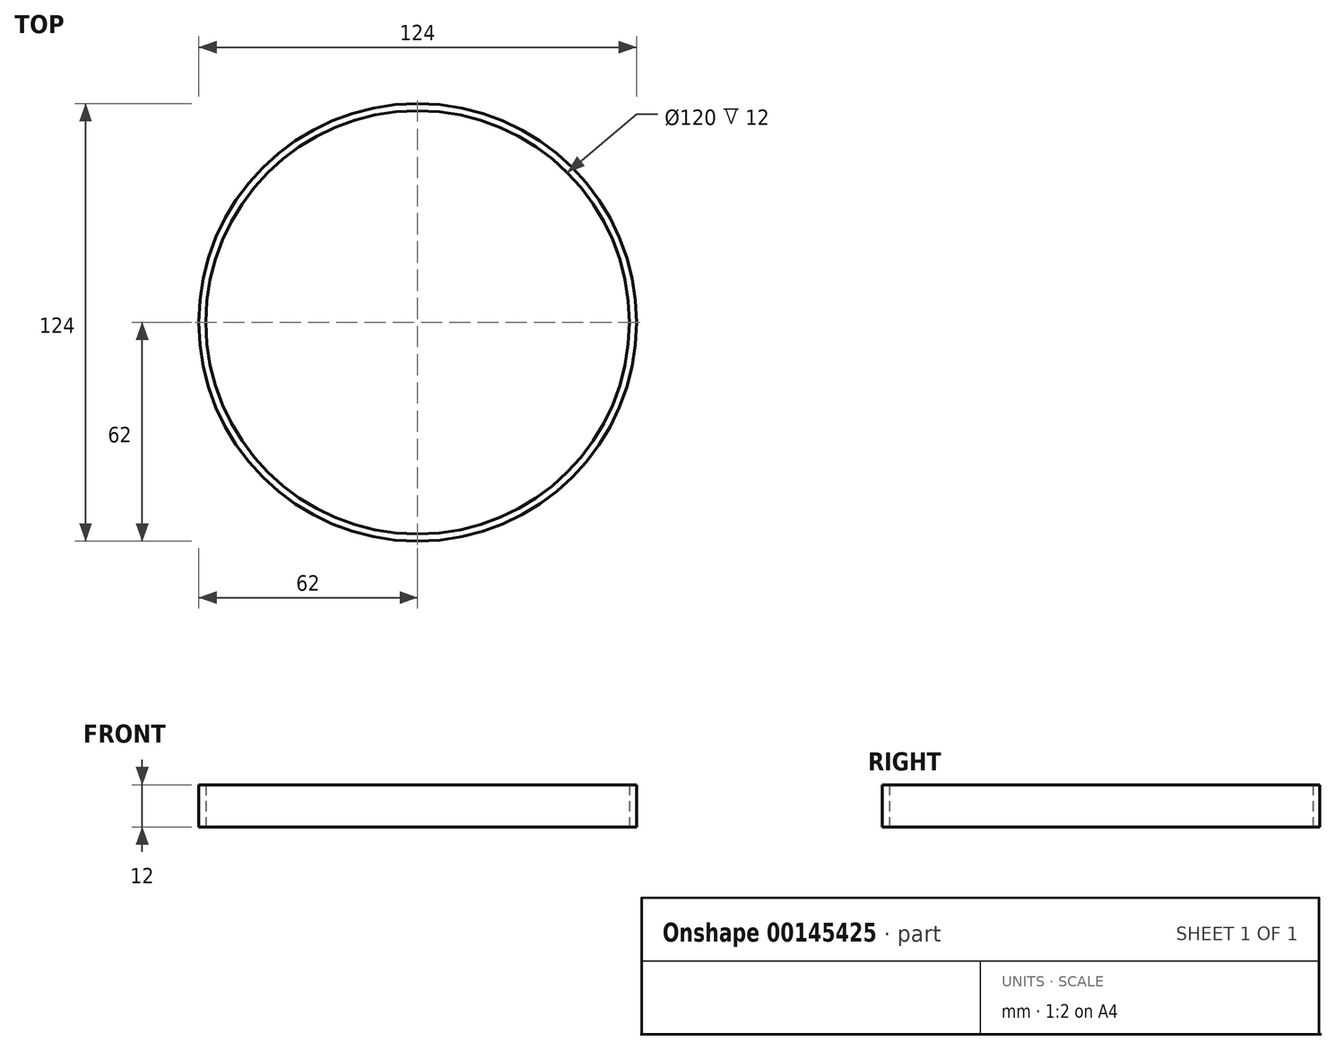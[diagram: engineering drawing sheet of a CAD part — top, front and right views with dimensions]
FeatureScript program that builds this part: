
annotation { "Feature Type Name" : "Feature", "Feature Type Description" : "" }
export const myFeature = defineFeature(function(context is Context, id is Id, definition is map)
    precondition{}
    {
        {
            var Q0;
            Q0=qCreatedBy(makeId("Top.planeOp"),FACE);
            var sketch = newSketch(context, id + "F0", { "sketchPlane" : qUnion([Q0])});
            skCircle(sketch, "E0", {"center": v(0, 0) * mm, "radius": 60 * mm});
            skCircle(sketch, "E1.0", {"center": v(0, 0) * mm, "radius": 62 * mm});
            skSolve(sketch);
        }
        {
            var Q0;
            Q0 = qSketchRegion(id + "F0", true);
            extrude(context, id + "F1", {"entities" : qUnion([Q0]), "offsetDistance" : 25 * mm, "depth" : 12 * mm});
        }
    });
